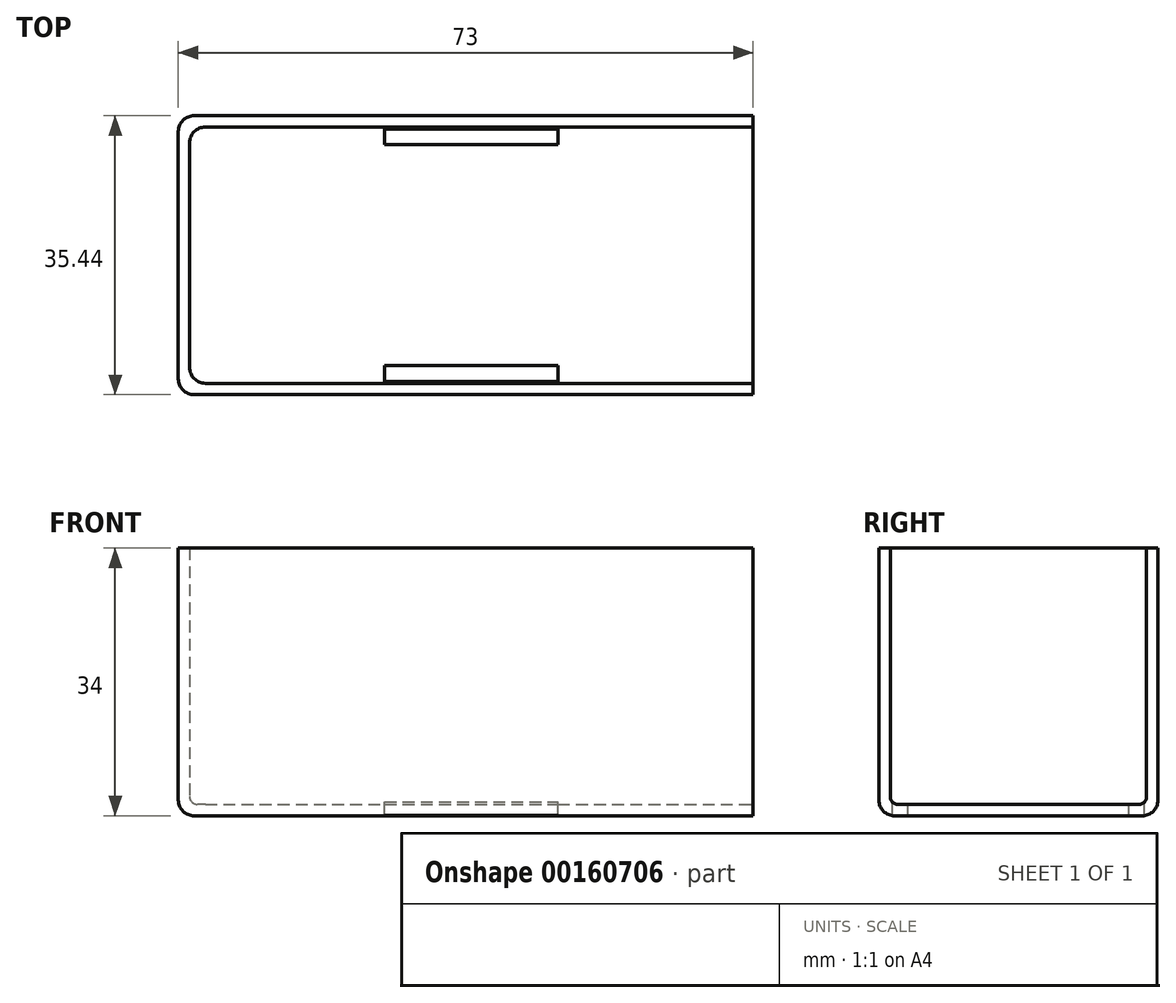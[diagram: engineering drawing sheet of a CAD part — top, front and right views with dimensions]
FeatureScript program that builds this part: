
annotation { "Feature Type Name" : "Feature", "Feature Type Description" : "" }
export const myFeature = defineFeature(function(context is Context, id is Id, definition is map)
    precondition{}
    {
        {
            var Q0;
            Q0=qCreatedBy(makeId("Top.planeOp"),FACE);
            var sketch = newSketch(context, id + "F0", { "sketchPlane" : qUnion([Q0])});
            skLineSegment(sketch, "E0.bottom", {"start": v(-37.22, 17.72) * mm, "end": v(37.22, 17.72) * mm});
            skLineSegment(sketch, "E0.top", {"start": v(-37.22, -17.72) * mm, "end": v(37.22, -17.72) * mm});
            skLineSegment(sketch, "E0.left", {"start": v(-37.22, 17.72) * mm, "end": v(-37.22, -17.72) * mm});
            skLineSegment(sketch, "E0.right", {"start": v(37.22, 17.72) * mm, "end": v(37.22, -17.72) * mm});
            skPoint(sketch, "E0.middle", {"position": v(0, 0) * mm});
            skSolve(sketch);
        }
        {
            var Q0;
            Q0 = qSketchRegion(id + "F0", true);
            extrude(context, id + "F1", {"entities" : qUnion([Q0]), "depth" : 34 * mm});
        }
        {
            var Q0;
            Q0=makeQuery(id+"F1.opExtrude","CAP_FACE",FACE,{"disambiguationData":[OSD([sQuery(id+"F0.wireOp",EDGE,"E0.bottom"),sQuery(id+"F0.wireOp",EDGE,"E0.top"),sQuery(id+"F0.wireOp",EDGE,"E0.left"),sQuery(id+"F0.wireOp",EDGE,"E0.right")])],"isStart":false});
            shell(context, id + "F2", {"entities" : qUnion([Q0]), "thickness" : 1.44 * mm});
        }
        {
            var Q0;
            Q0=makeQuery(id+"F1.opExtrude","SWEPT_FACE",FACE,{"disambiguationData":[OSD([sQuery(id+"F0.wireOp",EDGE,"E0.right")])]});
            extrude(context, id + "F3", {"entities" : qUnion([Q0]), "operationType" : NewBodyOperationType.REMOVE, "oppositeDirection" : true, "depth" : 1.44 * mm});
        }
        {
            var Q0;
            Q0=makeQuery(id+"F2.opShell","OFFSET_EDGE",EDGE,{"disambiguationData":[OSD([sQuery(id+"F0.wireOp",EDGE,"E0.top"),sQuery(id+"F0.wireOp",EDGE,"E0.left")])]});
            var Q1;
            Q1=makeQuery(id+"F2.opShell","OFFSET_EDGE",EDGE,{"disambiguationData":[OSD([sQuery(id+"F0.wireOp",EDGE,"E0.bottom"),sQuery(id+"F0.wireOp",EDGE,"E0.left")])]});
            var Q2;
            Q2=makeQuery(id+"F1.opExtrude","SWEPT_EDGE",EDGE,{"disambiguationData":[OSD([sQuery(id+"F0.wireOp",EDGE,"E0.bottom"),sQuery(id+"F0.wireOp",EDGE,"E0.left")])]});
            var Q3;
            Q3=makeQuery(id+"F1.opExtrude","SWEPT_EDGE",EDGE,{"disambiguationData":[OSD([sQuery(id+"F0.wireOp",EDGE,"E0.top"),sQuery(id+"F0.wireOp",EDGE,"E0.left")])]});
            fillet(context, id + "F4", {"entities" : qUnion([Q0, Q1, Q2, Q3]), "radius" : 2 * mm, "tangentPropagation" : true, "allowEdgeOverflow" : false});
        }
        {
            var Q0;
            Q0=makeQuery(id+"F1.opExtrude","CAP_EDGE",EDGE,{"disambiguationData":[OSD([sQuery(id+"F0.wireOp",EDGE,"E0.left")])],"isStart":true});
            var Q1;
            Q1=makeQuery(id+"F1.opExtrude","CAP_EDGE",EDGE,{"disambiguationData":[OSD([sQuery(id+"F0.wireOp",EDGE,"E0.top")])],"isStart":true});
            var Q2;
            Q2=makeQuery(id+"F1.opExtrude","CAP_EDGE",EDGE,{"disambiguationData":[OSD([sQuery(id+"F0.wireOp",EDGE,"E0.bottom")])],"isStart":true});
            fillet(context, id + "F5", {"entities" : qUnion([Q0, Q1, Q2]), "radius" : 2 * mm, "allowEdgeOverflow" : false});
        }
        {
            var Q0;
            Q0=makeQuery(id+"F2.opShell","OFFSET_FACE",FACE,{"disambiguationData":[OSD([sQuery(id+"F0.wireOp",EDGE,"E0.bottom"),sQuery(id+"F0.wireOp",EDGE,"E0.top"),sQuery(id+"F0.wireOp",EDGE,"E0.left"),sQuery(id+"F0.wireOp",EDGE,"E0.right")])]});
            var sketch = newSketch(context, id + "F6", { "sketchPlane" : qUnion([Q0])});
            skLineSegment(sketch, "E1.bottom", {"start": v(-11, 14.03) * mm, "end": v(11, 14.03) * mm});
            skLineSegment(sketch, "E1.top", {"start": v(-11, 16.03) * mm, "end": v(11, 16.03) * mm});
            skLineSegment(sketch, "E1.left", {"start": v(-11, 14.03) * mm, "end": v(-11, 16.03) * mm});
            skLineSegment(sketch, "E1.right", {"start": v(11, 14.03) * mm, "end": v(11, 16.03) * mm});
            skPoint(sketch, "E1.middle", {"position": v(0, 15.03) * mm});
            skLineSegment(sketch, "E2.MirrorCS", {"start": v(-11, -14.03) * mm, "end": v(11, -14.03) * mm});
            skLineSegment(sketch, "E3.MirrorCS", {"start": v(-11, -14.03) * mm, "end": v(-11, -16.03) * mm});
            skLineSegment(sketch, "E4.MirrorCS", {"start": v(-11, -16.03) * mm, "end": v(11, -16.03) * mm});
            skLineSegment(sketch, "E5.MirrorCS", {"start": v(11, -14.03) * mm, "end": v(11, -16.03) * mm});
            skSolve(sketch);
        }
        {
            var Q0;
            Q0 = qSketchRegion(id + "F6", true);
            extrude(context, id + "F7", {"entities" : qUnion([Q0]), "operationType" : NewBodyOperationType.REMOVE, "endBound" : BoundingType.THROUGH_ALL, "oppositeDirection" : true, "depth" : 25 * mm});
        }
        {
            var Q0;
            {var subQ0=sQuery(id+"F0.wireOp",EDGE,"E0.top");Q0=makeQuery(id+"F2.opShell","OFFSET_EDGE",EDGE,{"disambiguationData":[OSD([subQ0]),TDD([makeQuery(id+"F1.opExtrude","CAP_EDGE",EDGE,{"disambiguationData":[OSD([subQ0])],"isStart":true})])]});}
            fillet(context, id + "F8", {"entities" : qUnion([Q0]), "radius" : 1 * mm, "tangentPropagation" : true, "allowEdgeOverflow" : false});
        }
    });
